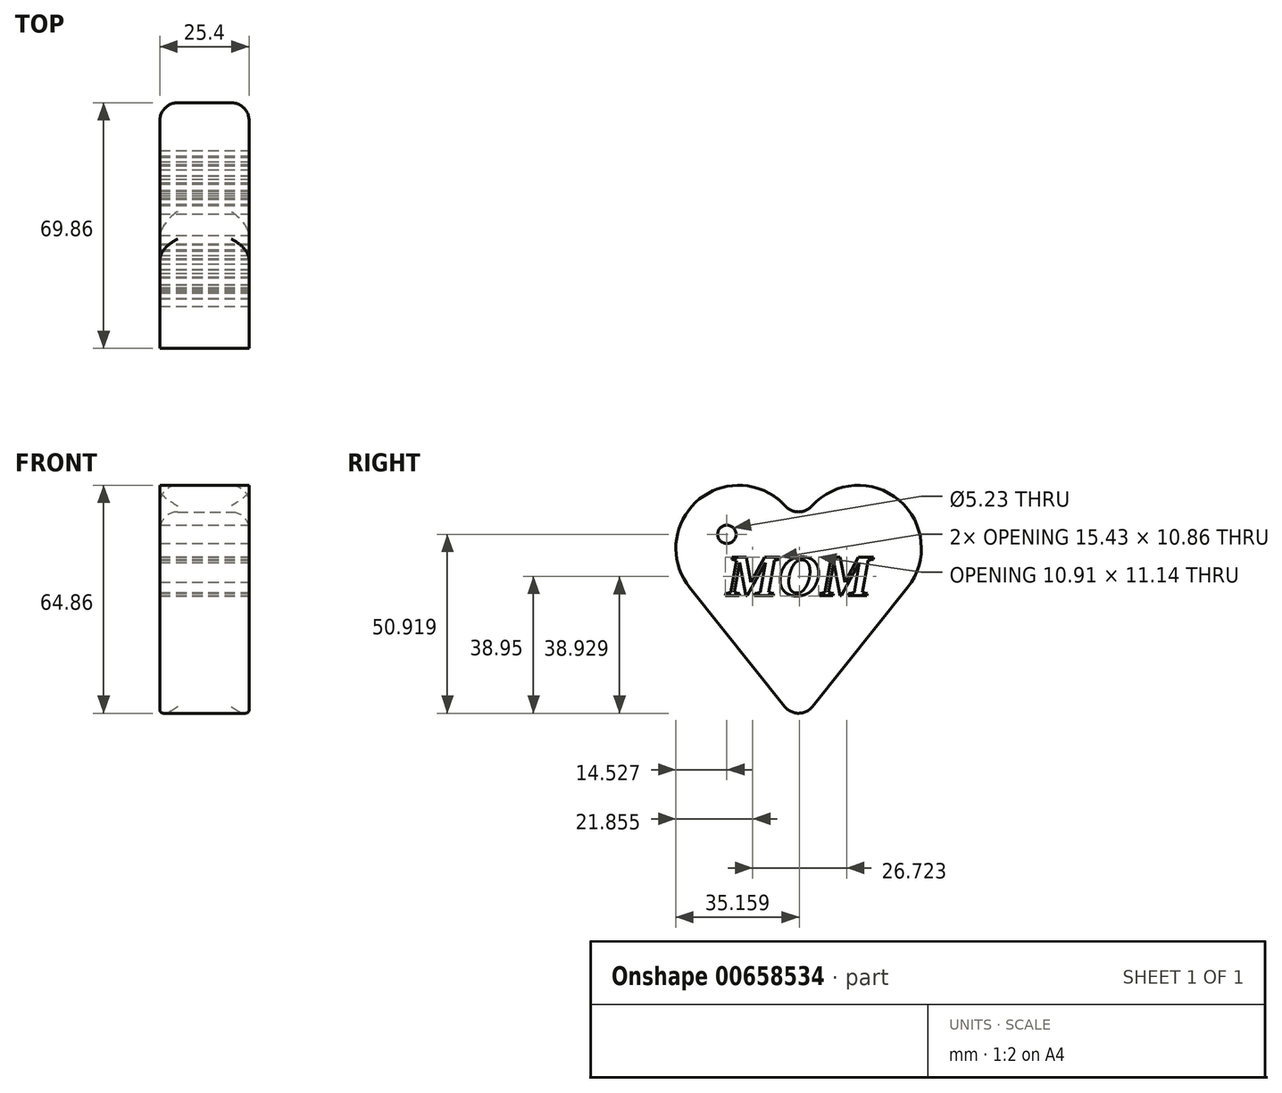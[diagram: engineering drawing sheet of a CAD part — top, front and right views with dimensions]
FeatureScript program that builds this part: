
annotation { "Feature Type Name" : "Feature", "Feature Type Description" : "" }
export const myFeature = defineFeature(function(context is Context, id is Id, definition is map)
    precondition{}
    {
        {
            var Q0;
            Q0=qCreatedBy(makeId("Right.planeOp"),FACE);
            var sketch = newSketch(context, id + "F0", { "sketchPlane" : qUnion([Q0])});
            skLineSegment(sketch, "E0", {"start": v(0, -38.87) * mm, "end": v(31.03, 0) * mm});
            skArc(sketch, "E1", {"start": v(31.03, 0) * mm, "mid": v(25.48, 26.94) * mm, "end": v(0, 16.6) * mm});
            skArc(sketch, "E2.MirrorCS", {"start": v(-31.03, 0) * mm, "mid": v(-25.48, 26.94) * mm, "end": v(0, 16.6) * mm});
            skLineSegment(sketch, "E3.MirrorCS", {"start": v(0, -38.87) * mm, "end": v(-31.03, 0) * mm});
            skSolve(sketch);
        }
        {
            var Q0;
            Q0=qSketchRegion(id+"F0",true);
            extrude(context, id + "F1", {"entities" : qUnion([Q0]), "depth" : 25.4 * mm, "offsetDistance" : 25.4 * mm});
        }
        {
            var Q0;
            Q0=makeQuery(id+"F1.opExtrude","CAP_FACE",FACE,{"disambiguationData":[OSD([sQuery(id+"F0.wireOp",EDGE,"E0"),sQuery(id+"F0.wireOp",EDGE,"E1"),sQuery(id+"F0.wireOp",EDGE,"E2.MirrorCS"),sQuery(id+"F0.wireOp",EDGE,"E3.MirrorCS")])],"isStart":false});
            var sketch = newSketch(context, id + "F2", { "sketchPlane" : qUnion([Q0])});
            skText(sketch, "E4", { "text": "MOM\n", "fontName": "Tinos-BoldItalic.ttf"});
            const initialGuessF2  = {"E4": [-0.02057, -0.00229, 1, 0, 0.01194]};
            skSetInitialGuess(sketch, initialGuessF2);
            skSolve(sketch);
        }
        {
            var Q0;
            Q0=qSketchRegion(id+"F2",true);
            extrude(context, id + "F3", {"entities" : qUnion([Q0]), "operationType" : NewBodyOperationType.REMOVE, "oppositeDirection" : true, "depth" : 152.4 * mm, "offsetDistance" : 25.4 * mm});
        }
        {
            var Q0;
            Q0=makeQuery(id+"F1.opExtrude","SWEPT_FACE",FACE,{"disambiguationData":[OSD([sQuery(id+"F0.wireOp",EDGE,"E1")])]});
            var Q1;
            Q1=makeQuery(id+"F1.opExtrude","SWEPT_EDGE",EDGE,{"disambiguationData":[OSD([sQuery(id+"F0.wireOp",EDGE,"E0"),sQuery(id+"F0.wireOp",EDGE,"E3.MirrorCS")])]});
            fillet(context, id + "F4", {"entities" : qUnion([Q0, Q1]), "radius" : 5.08 * mm, "tangentPropagation" : true, "allowEdgeOverflow" : false});
        }
        {
            var Q0;
            {var subQ0=sQuery(id+"F0.wireOp",EDGE,"E2.MirrorCS");var subQ1=sQuery(id+"F0.wireOp",EDGE,"E0");var subQ2=sQuery(id+"F0.wireOp",EDGE,"E3.MirrorCS");var subQ3=sQuery(id+"F0.wireOp",EDGE,"E1");Q0=makeQuery(id+"F3.boolean.opBoolean","SPLIT",FACE,{"disambiguationData":[TD([makeQuery(id+"F1.opExtrude","SWEPT_FACE",FACE,{"disambiguationData":[OSD([subQ1])]})])],"derivedFrom":makeQuery(id+"F1.opExtrude","CAP_FACE",FACE,{"disambiguationData":[OSD([subQ1,subQ3,subQ0,subQ2])],"isStart":false})});}
            var sketch = newSketch(context, id + "F5", { "sketchPlane" : qUnion([Q0])});
            skCircle(sketch, "E5", {"center": v(-20.4, 15.1) * mm, "radius": 2.62 * mm});
            skSolve(sketch);
        }
        {
            var Q0;
            Q0=makeQuery(id+"F5.imprint","IMPRINT",FACE,{"disambiguationData":[TD([[makeQuery(id+"F5.imprint","IMPRINT",EDGE,{"derivedFrom":sQuery(id+"F5.wireOp",EDGE,"E5")}),1.0]])]});
            extrude(context, id + "F6", {"entities" : qUnion([Q0]), "operationType" : NewBodyOperationType.REMOVE, "oppositeDirection" : true, "depth" : 152.4 * mm, "offsetDistance" : 25.4 * mm});
        }
    });
